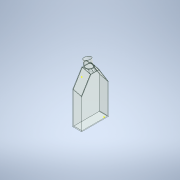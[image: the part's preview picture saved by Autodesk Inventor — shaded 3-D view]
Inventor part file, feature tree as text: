
AUTODESK INVENTOR PART (.ipt)
format: ipt  version: 2020 (Build 240168000, 168)  size: 654,848 bytes
history: native  units: in
note: dims shown in document units (in); Inventor stores cm internally (conversion verified against a paired STEP export)
features: sketch x27, extrude x14, projected_geometry x10, fillet x7, plane x4, sweep x2, loft x2, other x2
ambient origin geometry x8: Origin, YZ Plane, XZ Plane, XY Plane, X Axis, Y Axis, Z Axis, Center Point
bodies: Solid1 (feature_tree), Solid2 (feature_tree), Solid3 (feature_tree)
feature tree (68):
  extrude  "Extrusion1"  Depth=1.3327in
  extrude  "Extrusion2"  Depth=0.065in
  extrude  "Extrusion3"  Depth=0.065in
  extrude  "Extrusion4"  Depth=0.065in TaperAngle=0.0deg
  extrude  "Extrusion5"  TaperAngle=0.0deg  [1 undecoded]
  sweep  "Sweep1"
  sweep  "Sweep2"
  fillet  "Fillet1"  Radius=0.065in
  fillet  "Fillet2"  Radius=2.4016in
  extrude  "Extrusion6"  Depth=1.4823in
  loft  "Loft3"
  sketch  "Sketch12"  dims[d35=0.4075in d36=0.3543in]
  extrude  "Extrusion7"  TaperAngle=0.0deg  [1 undecoded]
  extrude  "Extrusion8"  Depth=0.0591in
  extrude  "Extrusion9"  Depth=0.3543in
  extrude  "Extrusion10"  Depth=0.1506in
  plane  "Work Plane2"
  sketch  "Sketch17"  dims[d45=0.065in d46=0.065in]
  plane  "Work Plane3"
  sketch  "Sketch18"  dims[d47=0.065in d52=0.0118in d53=0.0in d58=0.0in d59=90.0deg d60=0.0in d61=90.0deg d62=0.0118in d63=0.0in d64=0.5787in d65=0.5906in]
  extrude  "Extrusion11"  Depth=1.1024in
  sketch  "Sketch20"  dims[d67=0.7087in]
  extrude  "Extrusion12"  Depth=0.8661in
  sketch  "Sketch22"  dims[d70=0.2087in]
  sketch  "Sketch23"  dims[d73=0.5187in]
  extrude  "Extrusion13"  Depth=0.065in
  plane  "Work Plane4"
  extrude  "Extrusion19"  Depth=0.065in
  loft  "Loft4"
  fillet  "Fillet6"  [1 undecoded]
  fillet  "Fillet7"  [1 undecoded]
  fillet  "Fillet9"  Radius=0.0118in
  fillet  "Fillet10"  Radius=0.5787in
  fillet  "Fillet11"  Radius=0.5906in
  sketch  "Sketch42"  dims[d78=0.0118in d79=0.0in d80=0.0118in d81=0.0in d82=0.0996in d83=0.878in d84=-2.126in d85=90.0deg d86=1.1575in d87=1.0374in d88=0.3937in d89=0.0in d90=0.0079in d91=0.0in d92=0.3937in d93=0.0in d113=-2.126in d116=0.3543in d117=0.5092in d118=0.0in d119=0.0689in d120=0.0689in d121=0.0in d122=90.0deg d123=0.0in d124=90.0deg d125=0.0394in d126=0.0787in d128=0.0394in d129=0.0039in d130=0.0039in]
  sketch  "Sketch1"  dims[d0=4.252in d1=1.3327in]
  sketch  "Sketch2"  dims[d3=0.065in d4=0.065in]
  projected_geometry  "Projected Loop1"
  sketch  "Sketch3"  dims[d5=0.065in d6=0.065in]
  sketch  "Sketch4"  dims[d7=5.2362in d8=0.0in d9=0.065in d10=0.0in]
  sketch  "Sketch5"  dims[d11=0.3465in d12=0.0in d13=0.0in]
  sketch  "Sketch6"  dims[d14=2.4016in d15=1.4173in]
  sketch  "Sketch7"  dims[d16=1.4823in d17=1.4823in d18=0.065in d19=0.0in d20=2.4016in]
  projected_geometry  "Projected Loop2"
  sketch  "Sketch8"  dims[d21=1.4173in d22=1.4823in]
  projected_geometry  "Projected Loop3"
  sketch  "Sketch9"  dims[d23=1.4823in d24=0.065in d25=0.0in]
  sketch  "Sketch10"  dims[d26=0.0in d27=0.0in d28=0.0in d29=0.0in]
  sketch  "Sketch11"  dims[d30=0.0591in d31=0.0591in]
  projected_geometry  "Projected Loop4"
  other  "Edges4"
  sketch  "Sketch13"  dims[d37=0.3543in d38=0.1506in]
  projected_geometry  "Projected Loop5"
  sketch  "Sketch14"  dims[d39=0.1506in d40=1.1024in]
  sketch  "Sketch15"  dims[d41=0.8661in d42=0.8661in]
  projected_geometry  "Projected Loop6"
  projected_geometry  "Projected Loop7"
  sketch  "Sketch16"  dims[d43=0.065in d44=0.065in]
  plane  "Work Plane1"
  sketch  "Sketch19"  dims[d66=0.7087in]
  sketch  "Sketch21"  dims[d68=0.2087in]
  projected_geometry  "Projected Loop8"
  projected_geometry  "Projected Loop9"
  sketch  "Sketch24"  dims[d74=0.0276in]
  sketch  "Sketch37"  dims[d75=0.0276in]
  projected_geometry  "Projected Loop14"
  sketch  "Sketch38"  dims[d76=0.0079in d77=0.0in]
  other  "Edges5"
note: 4 required parameter values undecoded (feature->parameter linkage not recoverable at this tier; creation-order binding heuristic only, values carry confidence <= 0.55)
